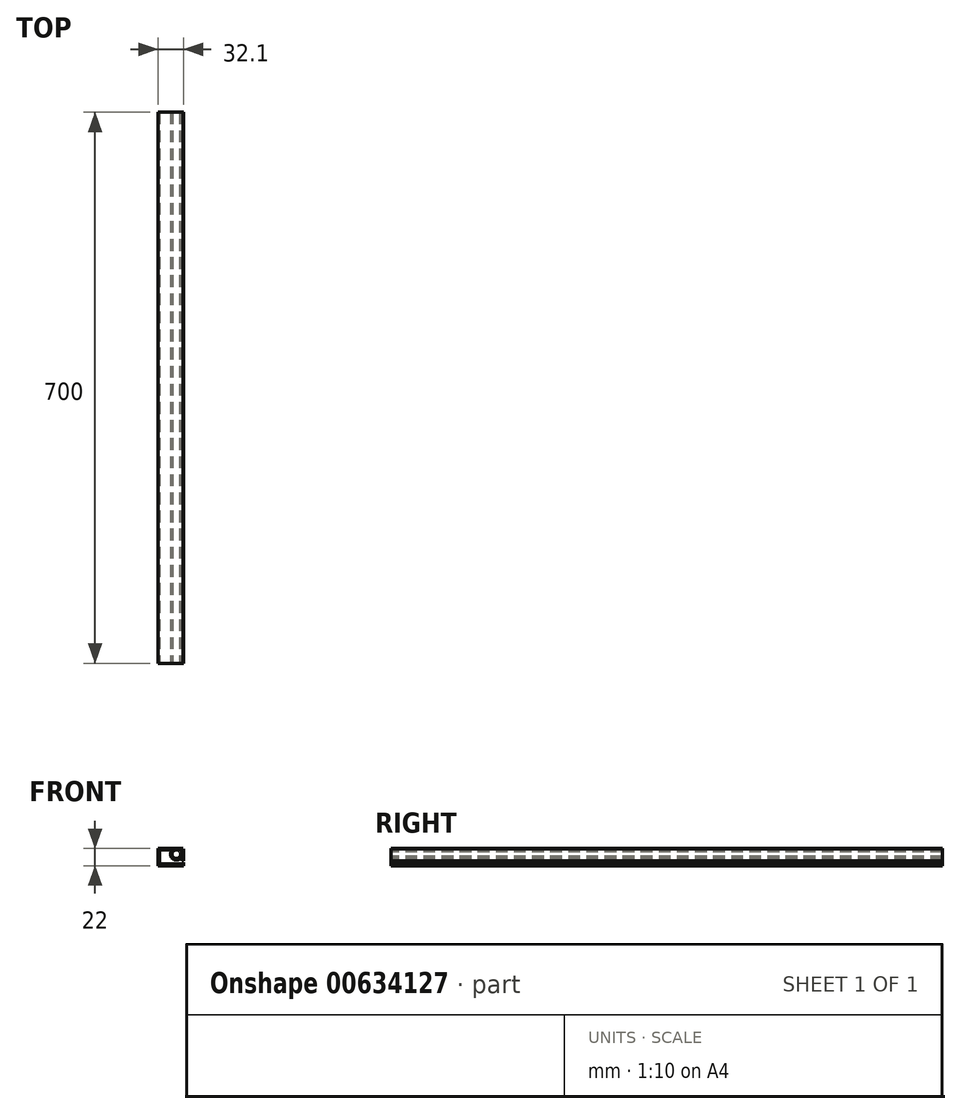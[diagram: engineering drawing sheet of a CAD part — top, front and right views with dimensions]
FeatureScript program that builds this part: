
annotation { "Feature Type Name" : "Feature", "Feature Type Description" : "" }
export const myFeature = defineFeature(function(context is Context, id is Id, definition is map)
    precondition{}
    {
        {
            var Q0;
            Q0=qCreatedBy(makeId("Front.planeOp"),FACE);
            var sketch = newSketch(context, id + "F0", { "sketchPlane" : qUnion([Q0])});
            skLineSegment(sketch, "E0.bottom", {"start": v(-15, 40) * mm, "end": v(15, 40) * mm});
            skLineSegment(sketch, "E0.top", {"start": v(-12, 0) * mm, "end": v(12, 0) * mm});
            skLineSegment(sketch, "E0.left", {"start": v(-15, 40) * mm, "end": v(-15, 37) * mm});
            skLineSegment(sketch, "E0.right", {"start": v(15, 37) * mm, "end": v(15, 3) * mm});
            skLineSegment(sketch, "E1.0", {"start": v(-15, 37) * mm, "end": v(3, 37) * mm});
            skLineSegment(sketch, "E1.1", {"start": v(-12, 6) * mm, "end": v(-12, 6) * mm});
            skLineSegment(sketch, "E1.2", {"start": v(-9, 3) * mm, "end": v(9, 3) * mm});
            skLineSegment(sketch, "E1.3", {"start": v(12, 29.6) * mm, "end": v(12, 6) * mm});
            skLineSegment(sketch, "E2.0", {"start": v(-15, 6) * mm, "end": v(-12, 6) * mm});
            skLineSegment(sketch, "E3", {"start": v(12, 40) * mm, "end": v(7.5, 40) * mm, "construction": true});
            skLineSegment(sketch, "E4", {"start": v(7, 34.8) * mm, "end": v(7, 40) * mm, "construction": true});
            skArc(sketch, "E5", {"start": v(7, 40) * mm, "mid": v(6.75, 29.6) * mm, "end": v(7.5, 39.98) * mm});
            skLineSegment(sketch, "E6.trimOffspring", {"start": v(-15, 6) * mm, "end": v(-15, 3) * mm});
            skPoint(sketch, "E7.orphan", {"position": v(5, 29.7) * mm});
            skPoint(sketch, "E8.visualSharp", {"position": v(15, 40) * mm});
            skArc(sketch, "E8.filletArc", {"start": v(15, 37) * mm, "mid": v(14.12, 39.12) * mm, "end": v(12, 40) * mm});
            skPoint(sketch, "E9.visualSharp", {"position": v(15, 0) * mm});
            skArc(sketch, "E9.filletArc", {"start": v(12, 0) * mm, "mid": v(14.12, 0.88) * mm, "end": v(15, 3) * mm});
            skArc(sketch, "E10.filletArc", {"start": v(9, 3) * mm, "mid": v(11.12, 3.88) * mm, "end": v(12, 6) * mm});
            skPoint(sketch, "E11.visualSharp", {"position": v(-12, 3) * mm});
            skArc(sketch, "E11.filletArc", {"start": v(-12, 6) * mm, "mid": v(-11.12, 3.88) * mm, "end": v(-9, 3) * mm});
            skPoint(sketch, "E12.visualSharp", {"position": v(-15, 0) * mm});
            skArc(sketch, "E12.filletArc", {"start": v(-15, 3) * mm, "mid": v(-14.12, 0.88) * mm, "end": v(-12, 0) * mm});
            skLineSegment(sketch, "E13.0", {"start": v(6.5, 34.8) * mm, "end": v(6.5, 39.8) * mm});
            skLineSegment(sketch, "E14.0", {"start": v(7.5, 34.8) * mm, "end": v(7.5, 40) * mm});
            skLineSegment(sketch, "E15", {"start": v(-15, 6) * mm, "end": v(-15, 16) * mm});
            skLineSegment(sketch, "E16", {"start": v(-15, 16) * mm, "end": v(-12, 16) * mm});
            skLineSegment(sketch, "E17", {"start": v(-12, 16) * mm, "end": v(-12, 6) * mm});
            skLineSegment(sketch, "E18", {"start": v(6.75, 29.6) * mm, "end": v(12, 29.6) * mm});
            skSolve(sketch);
        }
        {
            var Q0;
            Q0=qCreatedBy(makeId("Front.planeOp"),FACE);
            var sketch = newSketch(context, id + "F1", { "sketchPlane" : qUnion([Q0])});
            skLineSegment(sketch, "E19.1.1", {"start": v(7.5, 40) * mm, "end": v(-15, 40) * mm});
            skLineSegment(sketch, "E19.1.2", {"start": v(-15, 40) * mm, "end": v(-15, 37) * mm});
            skArc(sketch, "E19.2.8", {"start": v(-15, 3) * mm, "mid": v(-14.12, 0.88) * mm, "end": v(-12, 0) * mm, "construction": true});
            skLineSegment(sketch, "E19.2.9", {"start": v(-12, 0) * mm, "end": v(-5, 0) * mm});
            skLineSegment(sketch, "E19.2.13", {"start": v(17, 40) * mm, "end": v(8.5, 40) * mm});
            skLineSegment(sketch, "E19.3.0", {"start": v(-15, 18) * mm, "end": v(-15, 7.7) * mm});
            skPoint(sketch, "E20.2", {"position": v(6.5, 37.3) * mm});
            skPoint(sketch, "E21.orphan", {"position": v(6.5, 39.8) * mm});
            skPoint(sketch, "E19.0.2.end.orphan", {"position": v(7, 40) * mm});
            skPoint(sketch, "E22.orphan", {"position": v(12, 29.6) * mm});
            skPoint(sketch, "E23.orphan", {"position": v(7.5, 34.8) * mm});
            skPoint(sketch, "E20.0.start.orphan", {"position": v(6.5, 34.8) * mm});
            skLineSegment(sketch, "E24", {"start": v(-15, 37) * mm, "end": v(-15, 31) * mm});
            skLineSegment(sketch, "E25", {"start": v(0, 0) * mm, "end": v(0, 15) * mm, "construction": true});
            skLineSegment(sketch, "E26", {"start": v(7.5, 40) * mm, "end": v(7.5, 37.97) * mm});
            skLineSegment(sketch, "E27", {"start": v(8.5, 40) * mm, "end": v(8.5, 37.97) * mm});
            skLineSegment(sketch, "E28", {"start": v(15, 32.5) * mm, "end": v(8, 32.5) * mm, "construction": true});
            skPoint(sketch, "E29.orphan", {"position": v(7.6, 39) * mm});
            skLineSegment(sketch, "E30", {"start": v(8, 39) * mm, "end": v(8, 32.5) * mm, "construction": true});
            skPoint(sketch, "E19.3.3.end.orphan", {"position": v(-15, 16) * mm});
            skPoint(sketch, "E19.3.3.start.orphan", {"position": v(-12, 16) * mm});
            skLineSegment(sketch, "E31", {"start": v(-15, 3) * mm, "end": v(-15, 0) * mm});
            skLineSegment(sketch, "E32", {"start": v(-12, 0) * mm, "end": v(-15, 0) * mm});
            skLineSegment(sketch, "E33", {"start": v(-15, 40) * mm, "end": v(-15, 31) * mm, "construction": true});
            skLineSegment(sketch, "E34", {"start": v(-15, 40) * mm, "end": v(-15, 31) * mm});
            skLineSegment(sketch, "E35.trimOffspring", {"start": v(-15, 31) * mm, "end": v(-15, 26) * mm});
            skLineSegment(sketch, "E36.trimOffspring", {"start": v(-15, 29) * mm, "end": v(-15, 24) * mm});
            skPoint(sketch, "E37.orphan", {"position": v(12, 40) * mm});
            skPoint(sketch, "E38.orphan", {"position": v(12, 0) * mm});
            skLineSegment(sketch, "E39.0", {"start": v(13.1, 38) * mm, "end": v(13.1, 38) * mm});
            skLineSegment(sketch, "E40.1", {"start": v(-13, 2) * mm, "end": v(-11, 2) * mm, "construction": true});
            skLineSegment(sketch, "E41.0", {"start": v(-13, 38) * mm, "end": v(-13, 34) * mm});
            skArc(sketch, "E42", {"start": v(13.32, 33.87) * mm, "mid": v(11.56, 36.69) * mm, "end": v(8.5, 37.97) * mm});
            skLineSegment(sketch, "E43.0", {"start": v(29.42, 20) * mm, "end": v(-7, 20) * mm, "construction": true});
            skLineSegment(sketch, "E44.trimOffspring", {"start": v(-13, 0.17) * mm, "end": v(-13, 0) * mm});
            skArc(sketch, "E45.0", {"start": v(2.9, 38) * mm, "mid": v(3.81, 26.3) * mm, "end": v(15, 29.84) * mm});
            skLineSegment(sketch, "E46.trimOffspring", {"start": v(2.9, 38) * mm, "end": v(-13, 38) * mm});
            skLineSegment(sketch, "E47.trimOffspring", {"start": v(13.32, 33.87) * mm, "end": v(13.43, 31.7) * mm});
            skArc(sketch, "E48.trimOffspring", {"start": v(13.1, 38) * mm, "mid": v(13.1, 38) * mm, "end": v(13.1, 38) * mm});
            skArc(sketch, "E49.trimOffspring", {"start": v(7.5, 37.97) * mm, "mid": v(4.01, 28.73) * mm, "end": v(13.43, 31.7) * mm});
            skPoint(sketch, "E50.orphan", {"position": v(7.5, 39) * mm});
            skPoint(sketch, "E51.start.orphan", {"position": v(8.5, 39) * mm});
            skLineSegment(sketch, "E52.0", {"start": v(8, 0) * mm, "end": v(8, 13.5) * mm});
            skLineSegment(sketch, "E53.0", {"start": v(-5, 0) * mm, "end": v(-5, 13.5) * mm});
            skLineSegment(sketch, "E54.0", {"start": v(16.47, 12) * mm, "end": v(14.46, 12) * mm, "construction": true});
            skLineSegment(sketch, "E55.trimOffspring", {"start": v(12.84, 12) * mm, "end": v(10, 12) * mm});
            skLineSegment(sketch, "E56.0", {"start": v(1.5, 0) * mm, "end": v(1.5, 20) * mm, "construction": true});
            skLineSegment(sketch, "E57", {"start": v(1.5, 20) * mm, "end": v(-9.16, 15.5) * mm});
            skLineSegment(sketch, "E58", {"start": v(1.5, 20) * mm, "end": v(10.84, 15.5) * mm});
            skLineSegment(sketch, "E59.0", {"start": v(-9.16, 13.5) * mm, "end": v(-5, 13.5) * mm});
            skLineSegment(sketch, "E60", {"start": v(-9.16, 15.5) * mm, "end": v(-9.16, 13.5) * mm});
            skLineSegment(sketch, "E61", {"start": v(10.84, 15.5) * mm, "end": v(10.84, 13.5) * mm});
            skLineSegment(sketch, "E62.trimOffspring", {"start": v(8, 13.5) * mm, "end": v(10.84, 13.5) * mm});
            skLineSegment(sketch, "E63.trimOffspring", {"start": v(10, 2) * mm, "end": v(15, 2) * mm});
            skLineSegment(sketch, "E64.trimOffspring", {"start": v(8, 0) * mm, "end": v(17, 0) * mm});
            skLineSegment(sketch, "E65.0", {"start": v(10, 2) * mm, "end": v(10, 12) * mm});
            skLineSegment(sketch, "E66.0", {"start": v(1.55, 22.2) * mm, "end": v(-7, 18.58) * mm});
            skLineSegment(sketch, "E66.1", {"start": v(1.55, 22.2) * mm, "end": v(12.84, 16.75) * mm});
            skLineSegment(sketch, "E67.0", {"start": v(-11.16, 16.82) * mm, "end": v(-11.16, 15.5) * mm});
            skLineSegment(sketch, "E68.0", {"start": v(-13, 11.5) * mm, "end": v(-7, 11.5) * mm});
            skLineSegment(sketch, "E69", {"start": v(-11.16, 15.5) * mm, "end": v(-11.16, 13.5) * mm});
            skLineSegment(sketch, "E70.0", {"start": v(12.84, 16.75) * mm, "end": v(12.84, 12) * mm});
            skLineSegment(sketch, "E71.0", {"start": v(-13, 6.7) * mm, "end": v(-7, 6.7) * mm, "construction": true});
            skLineSegment(sketch, "E72.0", {"start": v(-15, 7.7) * mm, "end": v(-13, 7.7) * mm});
            skLineSegment(sketch, "E73.0", {"start": v(-15, 5.7) * mm, "end": v(-11, 5.7) * mm});
            skLineSegment(sketch, "E74.0", {"start": v(-15, 3.7) * mm, "end": v(-13, 3.7) * mm, "construction": true});
            skLineSegment(sketch, "E75.trimOffspring", {"start": v(-15, 5.7) * mm, "end": v(-15, 3) * mm});
            skLineSegment(sketch, "E76.trimOffspring", {"start": v(-13, 3.7) * mm, "end": v(-13, 2) * mm, "construction": true});
            skLineSegment(sketch, "E77.trimOffspring", {"start": v(-11, 5.7) * mm, "end": v(-11, 2) * mm});
            skLineSegment(sketch, "E78.0", {"start": v(-13, 13.5) * mm, "end": v(-11.16, 13.5) * mm});
            skLineSegment(sketch, "E79.trimOffspring", {"start": v(-9.16, 13.5) * mm, "end": v(-7, 13.5) * mm});
            skLineSegment(sketch, "E80.trimOffspring", {"start": v(-13, 11.5) * mm, "end": v(-13, 7.7) * mm});
            skLineSegment(sketch, "E81.0", {"start": v(-7, 11.5) * mm, "end": v(-7, 3.7) * mm});
            skLineSegment(sketch, "E82.trimOffspring", {"start": v(-11, 3.7) * mm, "end": v(-7, 3.7) * mm});
            skLineSegment(sketch, "E83.0", {"start": v(17, 40) * mm, "end": v(17, 0) * mm});
            skPoint(sketch, "E84.orphan", {"position": v(17.1, 0) * mm});
            skLineSegment(sketch, "E85.trimOffspring", {"start": v(15, 29.84) * mm, "end": v(15, 2) * mm});
            skPoint(sketch, "E86.start.orphan", {"position": v(15, 40) * mm});
            skLineSegment(sketch, "E87", {"start": v(-13, 13.5) * mm, "end": v(-13, 18) * mm});
            skLineSegment(sketch, "E88.trimOffspring", {"start": v(-15, 22) * mm, "end": v(-15, 21.16) * mm, "construction": true});
            skLineSegment(sketch, "E89.trimOffspring", {"start": v(-15, 22) * mm, "end": v(-15, 18) * mm});
            skPoint(sketch, "E90.start.orphan", {"position": v(-12, 28) * mm});
            skPoint(sketch, "E91.orphan", {"position": v(-12, 29) * mm});
            skLineSegment(sketch, "E92.0", {"start": v(-9, 26) * mm, "end": v(-11, 26) * mm});
            skLineSegment(sketch, "E93.0", {"start": v(-11, 24) * mm, "end": v(-13, 24) * mm});
            skLineSegment(sketch, "E94", {"start": v(-9, 20) * mm, "end": v(-9, 26) * mm});
            skLineSegment(sketch, "E95.0", {"start": v(-11, 20) * mm, "end": v(-11, 22) * mm});
            skLineSegment(sketch, "E96.trimOffspring", {"start": v(-11, 24) * mm, "end": v(-11, 26) * mm});
            skLineSegment(sketch, "E97.trimOffspring", {"start": v(-13, 28) * mm, "end": v(-13, 34) * mm});
            skLineSegment(sketch, "E98", {"start": v(-15, 22) * mm, "end": v(-11, 22) * mm});
            skLineSegment(sketch, "E99", {"start": v(-13, 24) * mm, "end": v(-15, 24) * mm});
            skLineSegment(sketch, "E100.0", {"start": v(-7, 18.58) * mm, "end": v(-7, 28) * mm});
            skLineSegment(sketch, "E101.0", {"start": v(-13, 18) * mm, "end": v(-8.36, 18) * mm});
            skLineSegment(sketch, "E102.trimOffspring", {"start": v(-8.36, 18) * mm, "end": v(-11.16, 16.82) * mm});
            skLineSegment(sketch, "E103.0", {"start": v(-11, 20) * mm, "end": v(-9, 20) * mm});
            skLineSegment(sketch, "E104.0", {"start": v(-7, 28) * mm, "end": v(-13, 28) * mm});
            skSolve(sketch);
        }
        {
            var Q0;
            Q0=qSketchRegion(id+"F1",true);
            extrude(context, id + "F2", {"entities" : qUnion([Q0]), "oppositeDirection" : true, "depth" : 1910 * mm, "offsetDistance" : 25 * mm});
        }
        {
            var Q0;
            Q0=makeQuery(id+"F1.imprint","IMPRINT",FACE,{"disambiguationData":[TD([[makeQuery(id+"F1.imprint","IMPRINT",EDGE,{"derivedFrom":sQuery(id+"F1.wireOp",EDGE,"E19.1.1")}),1.0]])]});
            var sketch = newSketch(context, id + "F3", { "sketchPlane" : qUnion([Q0])});
            skLineSegment(sketch, "E105.0", {"start": v(-13.5, 18) * mm, "end": v(-13.5, -0.51) * mm});
            skSolve(sketch);
        }
        {
            var Q0;
            Q0=makeQuery(id+"F3.imprint","IMPRINT",FACE,{"disambiguationData":[TD([[makeQuery(id+"F3.imprint","IMPRINT",EDGE,{"derivedFrom":makeQuery(id+"F1.imprint","IMPRINT",EDGE,{"derivedFrom":sQuery(id+"F1.wireOp",EDGE,"E19.1.1")})}),1.0]])]});
            var sketch = newSketch(context, id + "F4", { "sketchPlane" : qUnion([Q0])});
            skLineSegment(sketch, "E106.0", {"start": v(-17, 40) * mm, "end": v(-25.5, 40) * mm});
            skLineSegment(sketch, "E107.0", {"start": v(-49.1, 40) * mm, "end": v(-49.1, 18) * mm});
            skLineSegment(sketch, "E108.0", {"start": v(-17, 40) * mm, "end": v(-17, 18) * mm});
            skPoint(sketch, "E109.orphan", {"position": v(7.5, 40) * mm});
            skLineSegment(sketch, "E110.1", {"start": v(-19, 29.83) * mm, "end": v(-19, 20) * mm});
            skLineSegment(sketch, "E110.3", {"start": v(-47.1, 38) * mm, "end": v(-47.1, 20) * mm});
            skArc(sketch, "E111.0", {"start": v(7.5, 37.97) * mm, "mid": v(4.01, 28.73) * mm, "end": v(13.43, 31.7) * mm, "construction": true});
            skLineSegment(sketch, "E112.0", {"start": v(17, 40) * mm, "end": v(8.5, 40) * mm});
            skLineSegment(sketch, "E113.0", {"start": v(7.5, 40) * mm, "end": v(-15, 40) * mm});
            skLineSegment(sketch, "E114.0", {"start": v(-26.6, 40) * mm, "end": v(-26.6, 37.97) * mm});
            skLineSegment(sketch, "E115.0", {"start": v(-25.5, 40) * mm, "end": v(-25.5, 37.98) * mm});
            skLineSegment(sketch, "E116.0", {"start": v(-7, 18.58) * mm, "end": v(-7, 28) * mm});
            skLineSegment(sketch, "E117", {"start": v(-47.1, 23.29) * mm, "end": v(15, 23.29) * mm, "construction": true});
            skPoint(sketch, "E118.orphan", {"position": v(-7, 23.29) * mm});
            skLineSegment(sketch, "E119", {"start": v(8, 32.5) * mm, "end": v(2.5, 32.5) * mm});
            skLineSegment(sketch, "E120.0", {"start": v(8, 39) * mm, "end": v(8, 32.5) * mm});
            skLineSegment(sketch, "E120.1", {"start": v(17, 40) * mm, "end": v(17, 0) * mm});
            skLineSegment(sketch, "E121.trimOffspring", {"start": v(-17, 32.5) * mm, "end": v(-26, 32.5) * mm, "construction": true});
            skArc(sketch, "E122", {"start": v(-26.6, 37.97) * mm, "mid": v(-25.95, 27.01) * mm, "end": v(-25.5, 37.98) * mm});
            skArc(sketch, "E123.0", {"start": v(-31.1, 38) * mm, "mid": v(-30.2, 26.3) * mm, "end": v(-19, 29.83) * mm});
            skLineSegment(sketch, "E124.trimOffspring", {"start": v(-26.6, 40) * mm, "end": v(-49.1, 40) * mm});
            skLineSegment(sketch, "E125.trimOffspring", {"start": v(-26.6, 27.05) * mm, "end": v(-26.6, 20) * mm, "construction": true});
            skLineSegment(sketch, "E126.trimOffspring", {"start": v(-25.5, 27.04) * mm, "end": v(-25.5, 20) * mm, "construction": true});
            skLineSegment(sketch, "E127.trimOffspring", {"start": v(-31.1, 38) * mm, "end": v(-47.1, 38) * mm});
            skLineSegment(sketch, "E128.0", {"start": v(-49.1, 18) * mm, "end": v(-17, 18) * mm});
            skPoint(sketch, "E129.orphan", {"position": v(-8.36, 18) * mm});
            skPoint(sketch, "E130.orphan", {"position": v(-13, 18) * mm});
            skLineSegment(sketch, "E131.0", {"start": v(-47.1, 20) * mm, "end": v(-19, 20) * mm});
            skSolve(sketch);
        }
        {
            var Q0;
            Q0=makeQuery(id+"F3.imprint","IMPRINT",FACE,{"disambiguationData":[TD([[makeQuery(id+"F3.imprint","IMPRINT",EDGE,{"derivedFrom":makeQuery(id+"F1.imprint","IMPRINT",EDGE,{"derivedFrom":sQuery(id+"F1.wireOp",EDGE,"E19.1.1")})}),1.0]])]});
            var sketch = newSketch(context, id + "F5", { "sketchPlane" : qUnion([Q0])});
            skLineSegment(sketch, "E132.0", {"start": v(-9, 20) * mm, "end": v(-9, 26) * mm});
            skLineSegment(sketch, "E132.2", {"start": v(-11, 24) * mm, "end": v(-11, 26) * mm});
            skLineSegment(sketch, "E132.3", {"start": v(-9, 26) * mm, "end": v(-11, 26) * mm});
            skLineSegment(sketch, "E132.4", {"start": v(-11, 24) * mm, "end": v(-13, 24) * mm});
            skLineSegment(sketch, "E132.6", {"start": v(-13, 24) * mm, "end": v(-19, 24) * mm});
            skLineSegment(sketch, "E132.7", {"start": v(-11, 20) * mm, "end": v(-11, 22) * mm});
            skLineSegment(sketch, "E132.8", {"start": v(-19, 22) * mm, "end": v(-11, 22) * mm});
            skLineSegment(sketch, "E133.0", {"start": v(-19, 22) * mm, "end": v(-19, 20) * mm});
            skPoint(sketch, "E134.orphan", {"position": v(-15, 24) * mm});
            skPoint(sketch, "E135.orphan", {"position": v(-19, 29.83) * mm});
            skLineSegment(sketch, "E136.0", {"start": v(-21, 26) * mm, "end": v(-21, 20) * mm});
            skLineSegment(sketch, "E137", {"start": v(-21, 26) * mm, "end": v(-19, 26) * mm});
            skLineSegment(sketch, "E138.0", {"start": v(-19, 26) * mm, "end": v(-19, 24) * mm});
            skPoint(sketch, "E139.orphan", {"position": v(-15, 22) * mm});
            skLineSegment(sketch, "E140", {"start": v(-21, 20) * mm, "end": v(-19, 20) * mm});
            skSolve(sketch);
        }
        {
            var Q0;
            Q0=makeQuery(id+"F4.imprint","IMPRINT",FACE,{"disambiguationData":[TD([[makeQuery(id+"F4.imprint","IMPRINT",EDGE,{"derivedFrom":sQuery(id+"F4.wireOp",EDGE,"E106.0")}),1.0]])]});
            var sketch = newSketch(context, id + "F6", { "sketchPlane" : qUnion([Q0])});
            skLineSegment(sketch, "E141.0.1", {"start": v(-25.5, 40) * mm, "end": v(-49.1, 40) * mm});
            skLineSegment(sketch, "E141.0.2", {"start": v(-49.1, 40) * mm, "end": v(-49.1, 18) * mm});
            skLineSegment(sketch, "E141.0.3", {"start": v(-49.1, 18) * mm, "end": v(-17, 18) * mm});
            skLineSegment(sketch, "E141.0.4", {"start": v(-17, 18) * mm, "end": v(-17, 22) * mm});
            skLineSegment(sketch, "E141.0.5", {"start": v(-17.78, 40) * mm, "end": v(-25.5, 40) * mm});
            skPoint(sketch, "E142.0", {"position": v(-30.2, 26.3) * mm});
            skArc(sketch, "E143.0", {"start": v(-31.1, 38) * mm, "mid": v(-30.2, 26.3) * mm, "end": v(-19, 29.83) * mm});
            skLineSegment(sketch, "E144.0", {"start": v(-47.1, 20) * mm, "end": v(-19, 20) * mm});
            skLineSegment(sketch, "E145.0", {"start": v(-47.1, 38) * mm, "end": v(-47.1, 20) * mm});
            skLineSegment(sketch, "E146.0", {"start": v(-19, 22) * mm, "end": v(-17, 22) * mm});
            skLineSegment(sketch, "E147.0", {"start": v(-17, 24) * mm, "end": v(-19, 24) * mm});
            skLineSegment(sketch, "E148.0", {"start": v(-19, 29.83) * mm, "end": v(-19, 24) * mm});
            skLineSegment(sketch, "E149.0", {"start": v(-31.1, 38) * mm, "end": v(-47.1, 38) * mm});
            skPoint(sketch, "E150.orphan", {"position": v(-13, 24) * mm});
            skPoint(sketch, "E151.orphan", {"position": v(-11, 22) * mm});
            skLineSegment(sketch, "E152.trimOffspring", {"start": v(-19, 22) * mm, "end": v(-19, 20) * mm});
            skLineSegment(sketch, "E153.trimOffspring", {"start": v(-17, 24) * mm, "end": v(-17, 39.35) * mm});
            skLineSegment(sketch, "E154", {"start": v(-26, 32.5) * mm, "end": v(-17, 40) * mm, "construction": true});
            skLineSegment(sketch, "E155.0", {"start": v(-21.48, 35.62) * mm, "end": v(-17, 39.35) * mm});
            skLineSegment(sketch, "E156.0", {"start": v(-22.12, 36.4) * mm, "end": v(-17.78, 40) * mm});
            skArc(sketch, "E157.converted", {"start": v(-21.48, 35.62) * mm, "mid": v(-30.22, 29) * mm, "end": v(-22.12, 36.4) * mm});
            skPoint(sketch, "E141.0.6.end.orphan", {"position": v(-25.5, 37.98) * mm});
            skPoint(sketch, "E141.0.0.end.orphan", {"position": v(-26.6, 40) * mm});
            skPoint(sketch, "E141.0.0.start.orphan", {"position": v(-26.6, 37.97) * mm});
            skSolve(sketch);
        }
        {
            var Q0;
            Q0=qSketchRegion(id+"F6",true);
            extrude(context, id + "F7", {"entities" : qUnion([Q0]), "oppositeDirection" : true, "depth" : 700 * mm, "offsetDistance" : 25 * mm});
        }
        {
            var Q0;
            Q0=makeQuery(id+"F1.imprint","IMPRINT",FACE,{"disambiguationData":[TD([[makeQuery(id+"F1.imprint","IMPRINT",EDGE,{"derivedFrom":sQuery(id+"F1.wireOp",EDGE,"E19.1.1")}),1.0]])]});
            var sketch = newSketch(context, id + "F8", { "sketchPlane" : qUnion([Q0])});
            skLineSegment(sketch, "E158.0", {"start": v(17, 40) * mm, "end": v(17, 0) * mm});
            skLineSegment(sketch, "E159.0", {"start": v(17, 40) * mm, "end": v(-15, 40) * mm});
            skLineSegment(sketch, "E159.1", {"start": v(-15, 0) * mm, "end": v(17, 0) * mm});
            skLineSegment(sketch, "E159.2", {"start": v(-15, 40) * mm, "end": v(-15, 3) * mm});
            skPoint(sketch, "E160.orphan", {"position": v(7.5, 40) * mm});
            skPoint(sketch, "E161.orphan", {"position": v(-15, 18) * mm});
            skPoint(sketch, "E162.orphan", {"position": v(-12, 0) * mm});
            skLineSegment(sketch, "E163.0", {"start": v(-15, 3) * mm, "end": v(-15, 0) * mm});
            skPoint(sketch, "E164.orphan", {"position": v(-15, 7.7) * mm});
            skPoint(sketch, "E165.orphan", {"position": v(-5, 0) * mm});
            skSolve(sketch);
        }
        {
            var Q0;
            Q0=qSketchRegion(id+"F8",true);
            extrude(context, id + "F9", {"entities" : qUnion([Q0]), "operationType" : NewBodyOperationType.REMOVE, "oppositeDirection" : true, "depth" : 2000 * mm, "offsetDistance" : 25 * mm});
        }
    });
